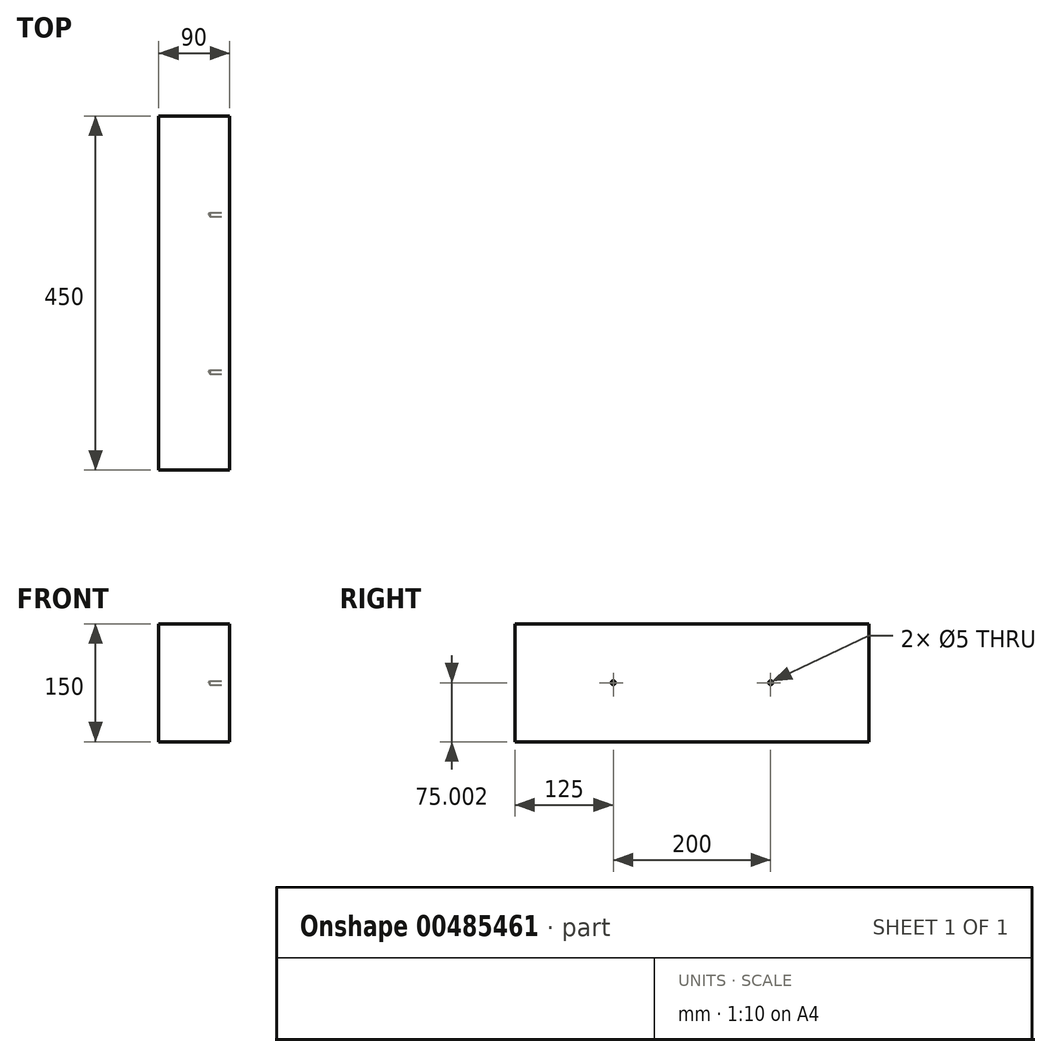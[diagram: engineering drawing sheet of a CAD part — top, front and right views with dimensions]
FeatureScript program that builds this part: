
annotation { "Feature Type Name" : "Feature", "Feature Type Description" : "" }
export const myFeature = defineFeature(function(context is Context, id is Id, definition is map)
    precondition{}
    {
        {
            var Q0;
            Q0=qCreatedBy(makeId("Front.planeOp"),FACE);
            var sketch = newSketch(context, id + "F0", { "sketchPlane" : qUnion([Q0])});
            skLineSegment(sketch, "E0.bottom", {"start": v(31.76, 21.1) * mm, "end": v(121.76, 21.1) * mm});
            skLineSegment(sketch, "E0.top", {"start": v(31.76, 171.1) * mm, "end": v(121.76, 171.1) * mm});
            skLineSegment(sketch, "E0.left", {"start": v(31.76, 21.1) * mm, "end": v(31.76, 171.1) * mm});
            skLineSegment(sketch, "E0.right", {"start": v(121.76, 21.1) * mm, "end": v(121.76, 171.1) * mm});
            skSolve(sketch);
        }
        {
            var Q0;
            Q0=qSketchRegion(id+"F0",true);
            extrude(context, id + "F1", {"entities" : qUnion([Q0]), "oppositeDirection" : true, "depth" : 450 * mm});
        }
        {
            var Q0;
            Q0=makeQuery(id+"F1.opExtrude","SWEPT_FACE",FACE,{"disambiguationData":[OSD([sQuery(id+"F0.wireOp",EDGE,"E0.right")])]});
            var sketch = newSketch(context, id + "F2", { "sketchPlane" : qUnion([Q0])});
            skPoint(sketch, "E1", {"position": v(125, 96.1) * mm});
            skPoint(sketch, "E2", {"position": v(325, 96.1) * mm});
            skSolve(sketch);
        }
        {
            var Q0;
            Q0=sQuery(id+"F2.wireOp",VERTEX,"E2");
            var Q1;
            Q1=sQuery(id+"F2.wireOp",VERTEX,"E1");
            var Q2;
            Q2=makeQuery(id+"F1.opExtrude","SWEPT_BODY",BODY,{"disambiguationData":[OSD([sQuery(id+"F0.wireOp",EDGE,"E0.bottom"),sQuery(id+"F0.wireOp",EDGE,"E0.top"),sQuery(id+"F0.wireOp",EDGE,"E0.left"),sQuery(id+"F0.wireOp",EDGE,"E0.right")])]});
            hole(context, id + "F3", {"style" : HoleStyle.SIMPLE, "endStyle" : HoleEndStyle.BLIND, "holeDiameter" : 5 * mm, "holeDepth" : 25 * mm, "isTappedThrough" : true, "tappedDepth" : 12 * mm, "tapClearance" : 3, "locations" : qUnion([Q0, Q1]), "scope" : qUnion([Q2])});
        }
    });
